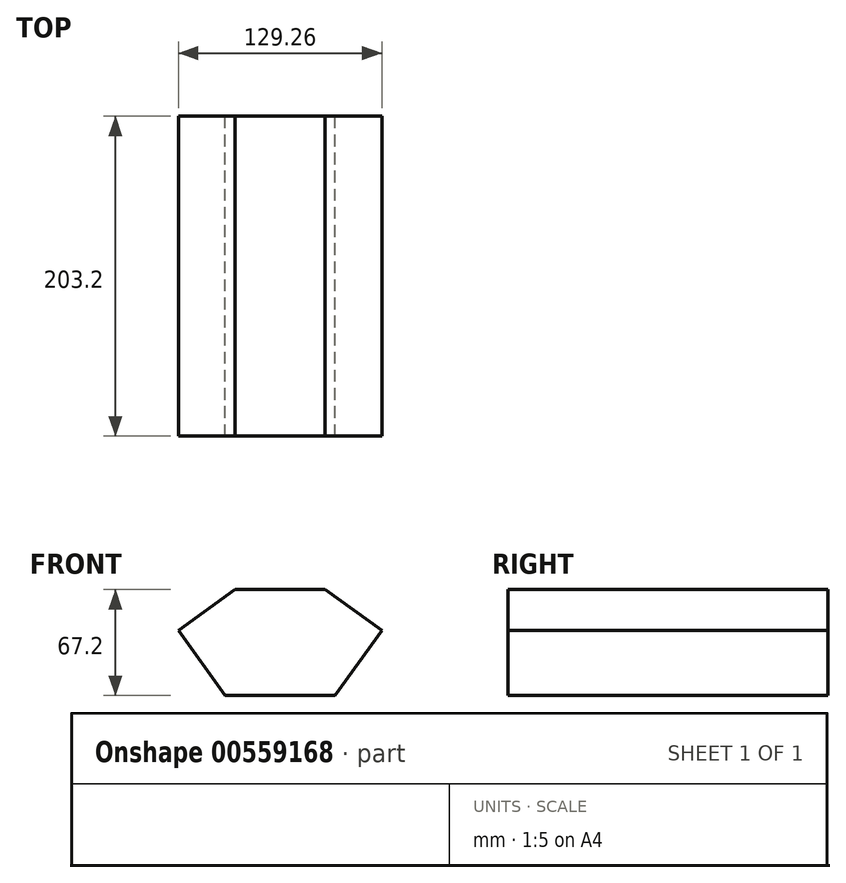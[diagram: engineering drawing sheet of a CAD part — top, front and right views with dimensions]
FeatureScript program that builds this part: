
annotation { "Feature Type Name" : "Feature", "Feature Type Description" : "" }
export const myFeature = defineFeature(function(context is Context, id is Id, definition is map)
    precondition{}
    {
        {
            var Q0;
            Q0=qCreatedBy(makeId("Front.planeOp"),FACE);
            var sketch = newSketch(context, id + "F0", { "sketchPlane" : qUnion([Q0])});
            skLineSegment(sketch, "E0", {"start": v(-34.93, 0) * mm, "end": v(34.93, 0) * mm});
            skLineSegment(sketch, "E1", {"start": v(-34.93, 0) * mm, "end": v(-64.63, 41.2) * mm});
            skLineSegment(sketch, "E2", {"start": v(-64.63, 41.2) * mm, "end": v(-28.58, 67.2) * mm});
            skLineSegment(sketch, "E3", {"start": v(-28.57, 67.2) * mm, "end": v(28.58, 67.2) * mm});
            skLineSegment(sketch, "E4", {"start": v(28.58, 67.2) * mm, "end": v(64.63, 41.2) * mm});
            skLineSegment(sketch, "E5", {"start": v(64.63, 41.2) * mm, "end": v(34.93, 0) * mm});
            skSolve(sketch);
        }
        {
            var Q0;
            Q0=makeQuery(id+"F0.imprint","IMPRINT",FACE,{"disambiguationData":[TD([[makeQuery(id+"F0.imprint","IMPRINT",EDGE,{"derivedFrom":sQuery(id+"F0.wireOp",EDGE,"E0")}),1.0]])]});
            extrude(context, id + "F1", {"entities" : qUnion([Q0]), "depth" : 203.2 * mm, "offsetDistance" : 25.4 * mm});
        }
    });
